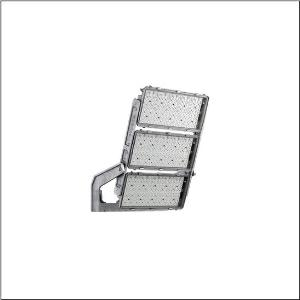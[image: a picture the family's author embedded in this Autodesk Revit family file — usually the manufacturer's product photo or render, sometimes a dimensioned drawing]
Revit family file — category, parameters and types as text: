
# Revit family: floodlight_fl_11_maxi_pro_remote___pl64_5xa779426v01aa_0b09
name_source: partatom
category: Lighting Fixtures
units: mm (PartAtom-declared; Revit-internal decimal feet)

## family parameters
Cut with Voids When Loaded = No
Host = Face
Light Source = No
Part Type = Normal
Room Calculation Point = No
Round Connector Dimension = Use Diameter
Shared = No

## types (1)
- --- (1 x LED, 216630 lm, 1539.7 W, 4000K)
    Apparent Load = 1540 VA
    CIE Flux Codes = 28 79 98 100 100
    Color Rendering = 70
    Color Temperature = 4000K
    Default Elevation = 1800 mm
    Description = Floodlight FL 11  maxi  pro Remote floodlight; light control with lens of PMMA; cover panel of toughened safety glass, transparent; light distribution: PL64, asymmetric direct distribution, LEDcolour temperature: 4000K, rated luminous flux: 216.630lm, colour rendering: CRI > 70, light colour: 740; luminous efficacy: 141lm/W; brightness control: DALI 2 (1 DALI address); with terminal, 8-pole, max. 2.5mm², mains connection: 220..240V/380..400V AC, 50/60Hz, surge voltage resistance: line to ground: 10kV, ECG replaceable separately, no afterglow with DALI off / DMX off command, LED unit replaceable without ESD environment, dustproof LED module, dimming range 10..100%; 1540W floodlight with 2x LED unit of diecast aluminium, coated grey; length: 713mm / width: 651mm / height: 338mm; mounting bracket, of diecast aluminium, uncoated, natural, equipment: Power, protection rating (complete): IP66; insulation class (complete): insulation class I (protective earthing); certification: CE, ENEC, VDE; ball protection: ball impact resistance with accessories, impact resistance: IK07; only for outdoor installations, rated ambient temperature 10°C, permissible operating ambient temperature: -40..+30°C, permissible storage temperature: -40..+85°C; packaging unit: 1 piece

Light Distribution: PL64
    Height = 320 mm
    Lamp = 1 x LED
    Lamp Light Flux = 216630 lm
    Lamp Power = 1539.7 W
    Lamp count = 1
    Length = 1002 mm
    Luminous efficacy = 141 lm/W
    Manufacturer = Siteco
    ModVariant = No
    Model = 5XA779426V01AA
    Mounting Place = Ceiling
    Mounting Type = Surface mounted
    Number of Poles = 1
    OnlyDefault = Yes
    Power Factor = 1
    Product Name = Floodlight FL 11 maxi pro Remote | PL64
    Product group = floodlight | ceiling mounted
    ProductGroupID = 303
    Protection Class = Protection class I
    Protection Degree = IP 66
    RLX_Detail_Level = 1
    RLX_Emergency_Light_Flux = 0 lm
    RLX_Emergency_Type = 0
    RLX_Emergency_Type_DB = No
    RlxData = <blob elided: 52261 chars, md5=3b67ee4d>
    Socket = socket
    Standby Power = 0 W
    System Light Flux = 216630 lm
    System Power = 1540 W
    Type Comments = factory setting: luminous flux: 100 % | dim-lin: 254 | 1080 mA
    Type Image = l_1006784.jpg
    URL = http://relux.com
    VarID = @adj_051311
    Voltage = 0 V
    Weight = 0.00 kg
    Width = 655 mm

## geometry (parser evidence)
native form markers: Blend x4, Sweep x13
no freeform markers — native parametric forms only
